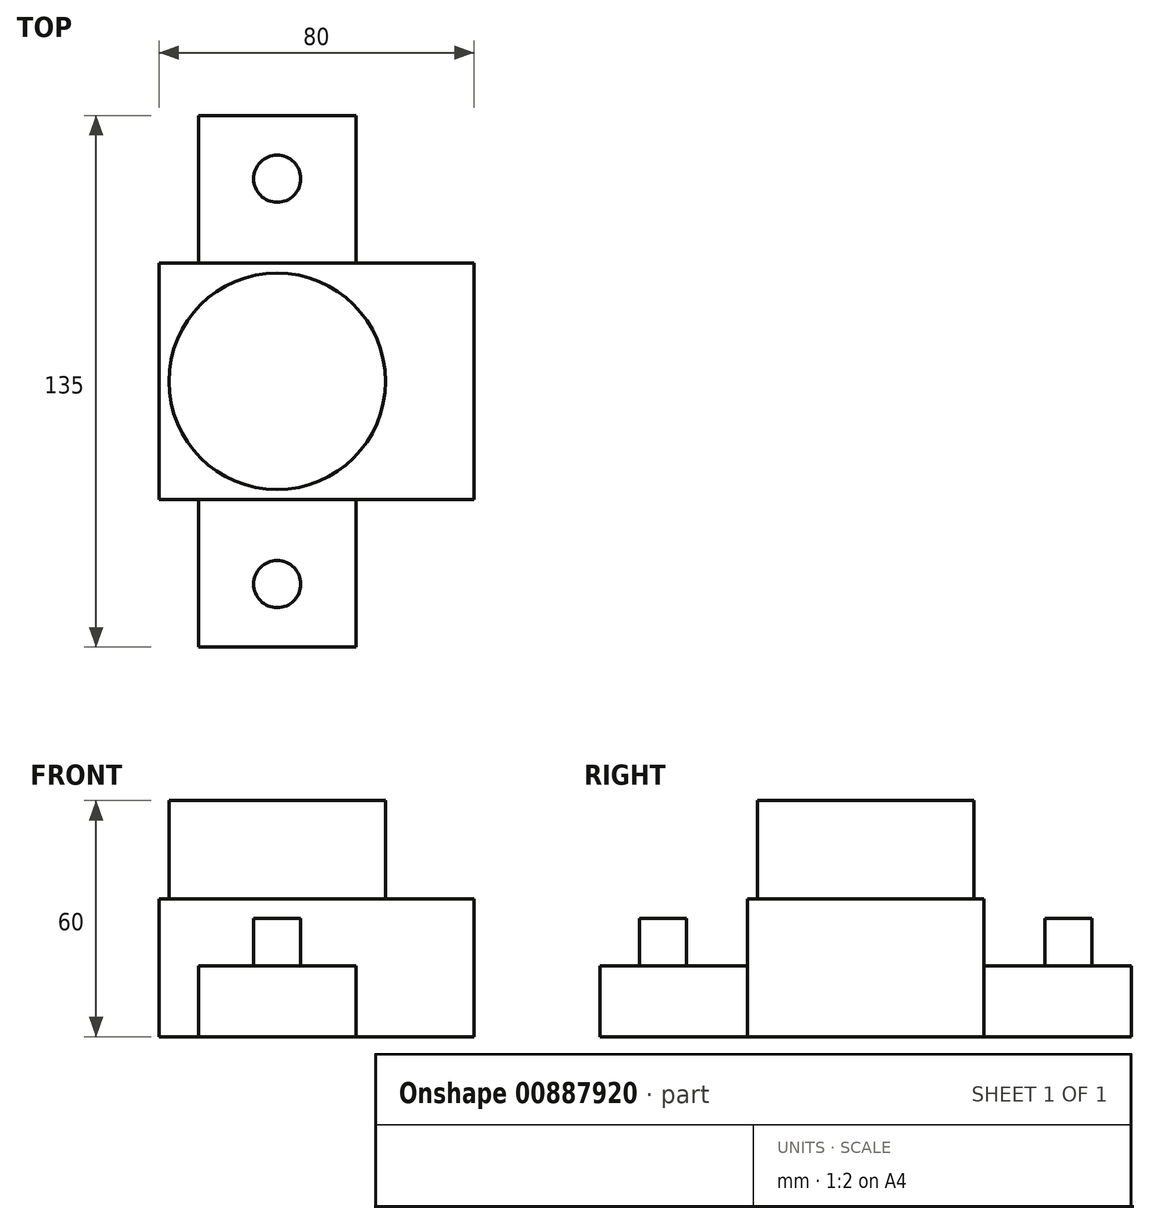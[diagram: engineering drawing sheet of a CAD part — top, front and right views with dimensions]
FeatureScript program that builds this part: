
annotation { "Feature Type Name" : "Feature", "Feature Type Description" : "" }
export const myFeature = defineFeature(function(context is Context, id is Id, definition is map)
    precondition{}
    {
        {
            var Q0;
            Q0=qCreatedBy(makeId("Top.planeOp"),FACE);
            var sketch = newSketch(context, id + "F0", { "sketchPlane" : qUnion([Q0])});
            skLineSegment(sketch, "E0.bottom", {"start": v(-20, 67.5) * mm, "end": v(20, 67.5) * mm});
            skLineSegment(sketch, "E0.top", {"start": v(-20, -67.5) * mm, "end": v(20, -67.5) * mm});
            skLineSegment(sketch, "E0.left", {"start": v(-20, 67.5) * mm, "end": v(-20, -67.5) * mm});
            skLineSegment(sketch, "E0.right", {"start": v(20, 67.5) * mm, "end": v(20, -67.5) * mm});
            skPoint(sketch, "E0.middle", {"position": v(0, 0) * mm});
            skSolve(sketch);
        }
        {
            var Q0;
            Q0 = qSketchRegion(id + "F0", true);
            extrude(context, id + "F1", {"entities" : qUnion([Q0]), "depth" : 30 * mm, "offsetDistance" : 25 * mm});
        }
        {
            var Q0;
            Q0=qCreatedBy(makeId("Top.planeOp"),FACE);
            var sketch = newSketch(context, id + "F2", { "sketchPlane" : qUnion([Q0])});
            skLineSegment(sketch, "E1.bottom", {"start": v(-30, 30) * mm, "end": v(50, 30) * mm});
            skLineSegment(sketch, "E1.top", {"start": v(-30, -30) * mm, "end": v(50, -30) * mm});
            skLineSegment(sketch, "E1.left", {"start": v(-30, 30) * mm, "end": v(-30, -30) * mm});
            skLineSegment(sketch, "E1.right", {"start": v(50, 30) * mm, "end": v(50, -30) * mm});
            skPoint(sketch, "E1.middle", {"position": v(10, 0) * mm});
            skSolve(sketch);
        }
        {
            var Q0;
            Q0=makeQuery(id+"F2.imprint","IMPRINT",FACE,{"disambiguationData":[TD([[makeQuery(id+"F2.imprint","IMPRINT",EDGE,{"derivedFrom":sQuery(id+"F2.wireOp",EDGE,"E1.bottom")}),-1.0]])]});
            extrude(context, id + "F3", {"entities" : qUnion([Q0]), "operationType" : NewBodyOperationType.ADD, "depth" : 60 * mm, "offsetDistance" : 25 * mm});
        }
        {
            var Q0;
            Q0=makeQuery(id+"F3.opExtrude","CAP_FACE",FACE,{"disambiguationData":[OSD([sQuery(id+"F2.wireOp",EDGE,"E1.bottom"),sQuery(id+"F2.wireOp",EDGE,"E1.top"),sQuery(id+"F2.wireOp",EDGE,"E1.left"),sQuery(id+"F2.wireOp",EDGE,"E1.right")])],"isStart":false});
            var sketch = newSketch(context, id + "F4", { "sketchPlane" : qUnion([Q0])});
            skLineSegment(sketch, "E2.bottom", {"start": v(-45.45, 38.01) * mm, "end": v(56.52, 38.01) * mm});
            skLineSegment(sketch, "E2.top", {"start": v(-45.45, -38.01) * mm, "end": v(56.52, -38.01) * mm});
            skLineSegment(sketch, "E2.left", {"start": v(-45.45, 38.01) * mm, "end": v(-45.45, -38.01) * mm});
            skLineSegment(sketch, "E2.right", {"start": v(56.52, 38.01) * mm, "end": v(56.52, -38.01) * mm});
            skPoint(sketch, "E2.middle", {"position": v(5.53, 0) * mm});
            skCircle(sketch, "E3", {"center": v(0, 0) * mm, "radius": 27.5 * mm});
            skSolve(sketch);
        }
        {
            var Q0;
            Q0=makeQuery(id+"F4.imprint","IMPRINT",FACE,{"disambiguationData":[TD([[makeQuery(id+"F4.imprint","IMPRINT",EDGE,{"derivedFrom":sQuery(id+"F4.wireOp",EDGE,"E3")}),-1.0]])]});
            extrude(context, id + "F5", {"entities" : qUnion([Q0]), "operationType" : NewBodyOperationType.REMOVE, "oppositeDirection" : true, "depth" : 25 * mm, "offsetDistance" : 25 * mm});
        }
        {
            var Q0;
            {var subQ0=sQuery(id+"F0.wireOp",EDGE,"E0.bottom");var subQ1=sQuery(id+"F0.wireOp",EDGE,"E0.right");var subQ2=sQuery(id+"F0.wireOp",EDGE,"E0.left");Q0=makeQuery(id+"F3.boolean.opBoolean","SPLIT",FACE,{"disambiguationData":[TD([makeQuery(id+"F1.opExtrude","SWEPT_FACE",FACE,{"disambiguationData":[OSD([subQ0])]})])],"derivedFrom":makeQuery(id+"F1.opExtrude","CAP_FACE",FACE,{"disambiguationData":[OSD([subQ0,sQuery(id+"F0.wireOp",EDGE,"E0.top"),subQ2,subQ1])],"isStart":false})});}
            var sketch = newSketch(context, id + "F6", { "sketchPlane" : qUnion([Q0])});
            skCircle(sketch, "E4", {"center": v(0, 51.5) * mm, "radius": 6 * mm});
            skLineSegment(sketch, "E5.bottom", {"start": v(-25.76, 72.06) * mm, "end": v(24.28, 72.06) * mm});
            skLineSegment(sketch, "E5.top", {"start": v(-25.76, 30) * mm, "end": v(24.28, 30) * mm});
            skLineSegment(sketch, "E5.left", {"start": v(-25.76, 72.06) * mm, "end": v(-25.76, 30) * mm});
            skLineSegment(sketch, "E5.right", {"start": v(24.28, 72.06) * mm, "end": v(24.28, 30) * mm});
            skLineSegment(sketch, "E6.MirrorCS", {"start": v(-25.76, -72.06) * mm, "end": v(24.28, -72.06) * mm});
            skLineSegment(sketch, "E7.MirrorCS", {"start": v(-25.76, -72.06) * mm, "end": v(-25.76, -30) * mm});
            skLineSegment(sketch, "E8.MirrorCS", {"start": v(24.28, -72.06) * mm, "end": v(24.28, -30) * mm});
            skCircle(sketch, "E9.MirrorC", {"center": v(0, -51.5) * mm, "radius": 6 * mm});
            skLineSegment(sketch, "E10.MirrorCS", {"start": v(-25.76, -30) * mm, "end": v(24.28, -30) * mm});
            skSolve(sketch);
        }
        {
            var Q0;
            Q0 = qSketchRegion(id + "F6", true);
            extrude(context, id + "F7", {"entities" : qUnion([Q0]), "operationType" : NewBodyOperationType.REMOVE, "oppositeDirection" : true, "depth" : 12 * mm, "offsetDistance" : 25 * mm});
        }
    });
